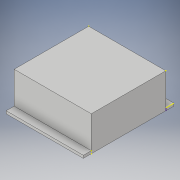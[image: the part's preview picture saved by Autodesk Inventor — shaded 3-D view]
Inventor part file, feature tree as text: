
AUTODESK INVENTOR PART (.ipt)
format: ipt  version: 2018 (Build 220112000, 112)  size: 146,944 bytes
history: native  units: in
note: dims shown in document units (in); Inventor stores cm internally (conversion verified against a paired STEP export)
features: sketch x8, extrude x5, projected_geometry x1
ambient origin geometry x8: Origin, YZ Plane, XZ Plane, XY Plane, X Axis, Y Axis, Z Axis, Center Point
bodies: Solid1 (feature_tree)
feature tree (14):
  extrude  "Extrusion1"  Depth=7.25in
  extrude  "Extrusion2"  Depth=0.25in
  extrude  "Extrusion3"  Depth=0.75in TaperAngle=0.0deg
  sketch  "Sketch4"  dims[d8=1.0in d9=3.0in]
  sketch  "Sketch5"  dims[d10=0.75in d11=0.0in d12=0.1in]
  extrude  "Extrusion4"  Depth=3.0in
  sketch  "Sketch7"  dims[d14=0.1in]
  extrude  "Extrusion5"  Depth=0.1in
  sketch  "Sketch1"  dims[d0=4.25in d1=7.25in]
  sketch  "Sketch2"  dims[d2=7.0in d3=0.0in d4=0.25in]
  sketch  "Sketch3"  dims[d5=1.0in d6=0.75in d7=0.0in]
  sketch  "Sketch6"  dims[d13=0.1in]
  sketch  "Sketch8"  dims[d15=0.0in d16=6.9in d17=0.0in d18=7.0in d19=0.0in]
  projected_geometry  "Projected Loop1"
